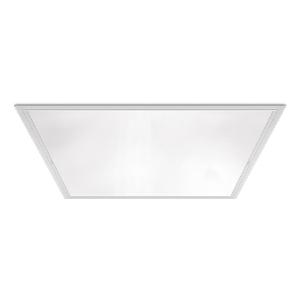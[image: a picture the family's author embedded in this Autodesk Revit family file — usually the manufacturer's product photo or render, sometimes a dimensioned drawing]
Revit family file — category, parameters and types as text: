
# Revit family: 3f_filippi_-_l_340_luce_diffusa_lgs_3f_filippi_-_23885_-_l_340_29w-940_dali_lgs_596x596
name_source: partatom
category: Lighting Fixtures
units: mm (PartAtom-declared; Revit-internal decimal feet)

## family parameters
Cut with Voids When Loaded = No
Host = Face
Light Source = No
Part Type = Normal
Room Calculation Point = No
Round Connector Dimension = Use Diameter
Shared = No

## types (1)
- 3F Filippi - L 340 Luce Diffusa LGS (1 x LED, 3413 lm, 35 W, 4000 K)
    Apparent Load = 35 VA
    Approval mark = ENEC
    CIE Flux Codes = 67 92 98 100 100
    Color Rendering = 90
    Color Temperature = 4000 K
    Control Gear = Electronic transformer
    Default Elevation = 1800 mm
    Description = ILLUMINOTECHNICAL
Luminous efficiency 100% (DLOR 100%, ULOR 0%).
Initial luminous flux of the luminaire 3413 lm.
Direct symmetric distribution.
Installation Interdistance Transv.D = 1.19 x hu - Long.D = 1.17 x hu.
Average luminance <1500 cd/m² for radial angles >65°.
Tabular UGR (CIE 117 - 4H-8H; S=0.25H; 70/50/20): RUG 16 - 16.1.
Beam angle: 87° - 86°.
Luminous efficacy 98 lm/W.
Lifetime (L93/B10): 30000 h. (tq+25°C)
Lifetime (L90/B10): 50000 h. (tq+25°C)
Lifetime (L85/B10): 80000 h. (tq+25°C)
Lifetime (L80/B10): 100000 h. (tq+25°C)
Sudden decreased luminous flux after 50000 hours: 0% (C0).
Photobiological safety in compliance with IEC/TR 62778: RG0 risk exempt, (IEC 62471).
In compliance with IEC/EN 62722-2-1 - IEC/EN 62717 standards.

SOURCE
Squared LED module 29W/940.
Energy efficiency class (UE 2019/2020 - UE 2019/2015): D.
CIE 13.3 Colour rendering index: CRI >90 (R9 >50%).
IES TM-30 Fidelity Index: Rf = 92 Rg = 101.
CCT nominal colour temperature 4000 K.
Colour initial tolerance (MacAdam): SDCM 3.

MECHANICAL
Housing in hot-galvanised steel, painted in white polyester.
Perimetral frame in white polycarbonate.
LGS micro-prismatic flat diffuser in transparent methacrylate (PMMA), multi-lenticular exterior, anti-glare.
Anti-glare opal polycarbonate filter for brightness uniformity.
Luminaire with limited surface temperature. - D - (EN 60598-2-24)
Dimensions: 596x596 mm, height 80 mm. Weight 4.4 kg.
IP40 protection degree.
Mechanical strength to impacts IK06 (1 joule).
Glow-wire test resistance 650°C.

ELECTRICAL
Wiring on a separate unit.
Halogen Free DALI-2 DATI (Parts 251, 252, 253), PUSH-DIM, electronic wiring 230V-50/60Hz, power factor 0.95 at full load, THD <25%, constant output current, SELV, class II, 1 driver, 1 DALI addresse.
Power of the luminaire 35 W.
CE - IEC 60598-1 - EN 60598-1.
SAFE FLICKER: PstLM=<1 and SVM=<0.4 (IEC TR 61547-1 and IEC TR 63158), to ensure a more comfortable and safe light.
Luminaire compliant with EN 60598-2-22 for power supply from a centralised emergency system CPSS (Central Power Supply System), not incorporated in the luminaire - high risk areas excluded. The default power and flux are 100% in AC and 100% in DC.
Ambient temperature from 0°C to +40°C.
Temperature class T6 max 85°C.
Relative humidity UR: <85%.

INSTALLATION
Lay-on or pull-up recessed fitting using frame accessory.
All accessories dedicated to this product are available on the Catalog and on our website www.3F-Filippi.com.

APPLICATIONS
Suitable product for food production plants (HACCP), IFS (Food Version 6), BRC (GSFS Food Version 7).
Environments: with VDTs, meeting rooms, offices.
Environments: architectural, commercial, staterooms, banks.
Environments where demanding visual tasks are performed and soft diffuse light is required for optimal visual comfort and total shielding of the light source.

LIGHT MANAGEMENT
Recommended minimum setting: 10%.
The luminaire, equipped with (DALI-2 DATI) driver, can be controlled manually with 3F Easy Dim technology or automatically/manually with wired or wireless DALI/D2D control systems.
The D2D driver guarantees interoperability with other devices with the same certification by making the following information available:
Device Data (Part 251), Energy Report (Part 252), Diagnosis & Maintenance (Part 253).
In electrical systems without a regulation system (manual or automatic) and DALI bus, a suitable jumper must be made on the DA-DA terminals of the appliance.

WARNING
Luminaire designed for disposal/recycling at end-of-life.
Replaceable (LED only) light source by a professional. Replaceable control gear by a professional.
    Height = 0 mm  [stored 0 ft]
    Lamp = 1 x LED
    Lamp Light Flux = 3413 lm
    Lamp Power = 35 W
    Lamp count = 1
    Length = 596 mm
    Lifetime = 50000 h
    Luminous efficacy = 98 lm/W
    Manufacturer = 3F Filippi
    ModVariant = No
    Model = 3F Filippi - 23885 - L 340 29W-940 DALI LGS 596x596
    Mounting Place = Ceiling
    Mounting Type = Recessed
    Number of Poles = 1
    OnlyDefault = Yes
    Power Factor = 1
    Product Name = 3F Filippi - L 340 Luce Diffusa LGS
    Product group = recessed luminaire
    ProductGroupID = 4
    Protection Class = Protection class II
    Protection Degree = IP 40
    RLX_Detail_Level = 1
    RLX_Emergency_Light_Flux = 0 lm
    RLX_Emergency_Type = 0
    RLX_Emergency_Type_DB = No
    RlxData = <blob elided: 156457 chars, md5=2c07a1d1>
    Socket = socket
    Standby Power = 0 W
    System Light Flux = 3413 lm
    System Power = 35 W
    Type Comments = Product without accessories
    Type Image = 3ffilippi_l_340_luce_diffusa_lgs.jpg
    URL = http://relux.com
    VarID = ---
    Voltage = 0 V
    Weight = 0.00 kg
    Width = 596 mm

note: [stored X ft] marks values corroborated as IEEE doubles in the binary element streams (Revit-internal decimal feet)

## geometry (parser evidence)
native form markers: Blend x4, Sweep x10
no freeform markers — native parametric forms only
